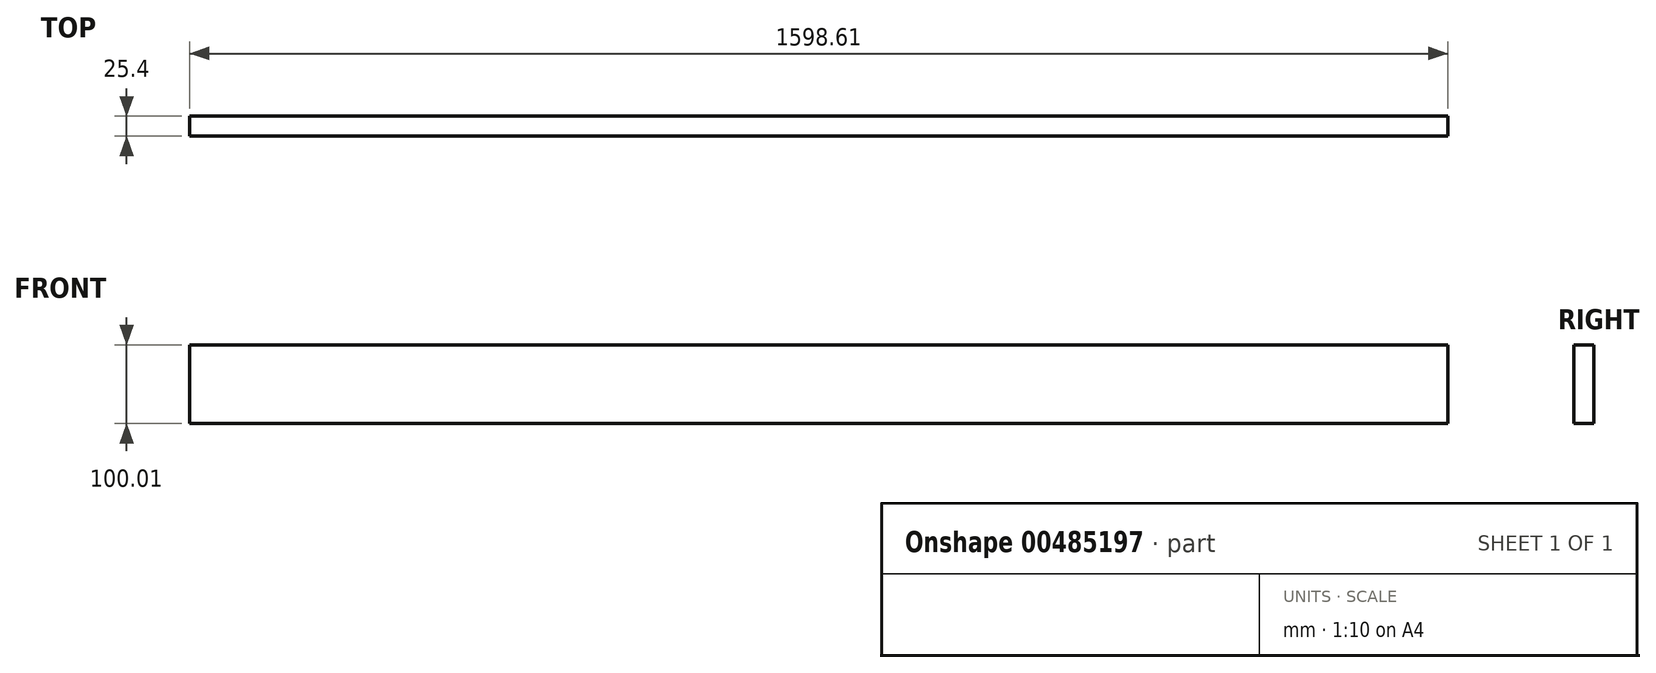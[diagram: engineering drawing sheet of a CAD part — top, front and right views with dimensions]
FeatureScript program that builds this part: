
annotation { "Feature Type Name" : "Feature", "Feature Type Description" : "" }
export const myFeature = defineFeature(function(context is Context, id is Id, definition is map)
    precondition{}
    {
        {
            var Q0;
            Q0=qCreatedBy(makeId("Front.planeOp"),FACE);
            var sketch = newSketch(context, id + "F0", { "sketchPlane" : qUnion([Q0])});
            skLineSegment(sketch, "E0.bottom", {"start": v(0, 0) * mm, "end": v(1598.61, 0) * mm});
            skLineSegment(sketch, "E0.top", {"start": v(0, -100.01) * mm, "end": v(1598.61, -100.01) * mm});
            skLineSegment(sketch, "E0.left", {"start": v(0, 0) * mm, "end": v(0, -100.01) * mm});
            skLineSegment(sketch, "E0.right", {"start": v(1598.61, 0) * mm, "end": v(1598.61, -100.01) * mm});
            skSolve(sketch);
        }
        {
            var Q0;
            Q0 = qSketchRegion(id + "F0", true);
            extrude(context, id + "F1", {"entities" : qUnion([Q0]), "oppositeDirection" : true, "depth" : 25.4 * mm});
        }
    });
